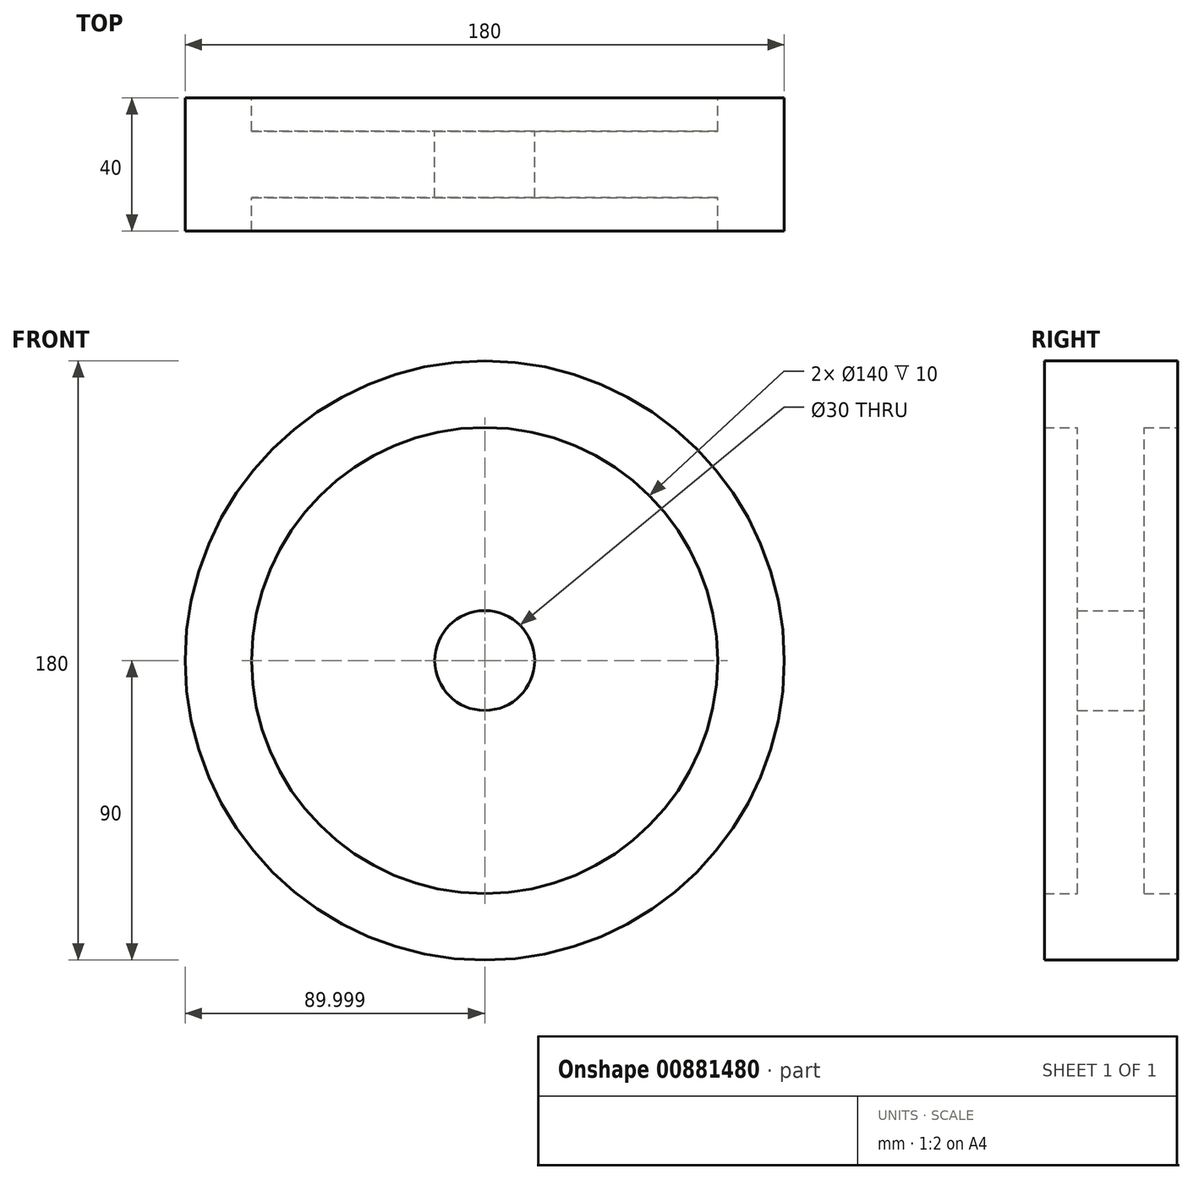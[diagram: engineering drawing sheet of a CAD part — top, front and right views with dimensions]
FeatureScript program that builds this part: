
annotation { "Feature Type Name" : "Feature", "Feature Type Description" : "" }
export const myFeature = defineFeature(function(context is Context, id is Id, definition is map)
    precondition{}
    {
        {
            var Q0;
            Q0=qCreatedBy(makeId("Front.planeOp"),FACE);
            var sketch = newSketch(context, id + "F0", { "sketchPlane" : qUnion([Q0])});
            skCircle(sketch, "E0", {"center": v(-22.68, 0) * mm, "radius": 15 * mm});
            skCircle(sketch, "E1", {"center": v(-22.68, 0) * mm, "radius": 90 * mm});
            skCircle(sketch, "E2.0", {"center": v(-22.68, 0) * mm, "radius": 70 * mm});
            skSolve(sketch);
        }
        {
            var Q0;
            Q0 = qSketchRegion(id + "F0", true);
            extrude(context, id + "F1", {"entities" : qUnion([Q0]), "depth" : 20 * mm, "offsetDistance" : 25 * mm, "hasSecondDirection" : true, "secondDirectionOppositeDirection" : true, "secondDirectionDepth" : 20 * mm});
        }
        {
            var Q0;
            Q0=makeQuery(id+"F0.imprint","IMPRINT",FACE,{"disambiguationData":[TD([[makeQuery(id+"F0.imprint","IMPRINT",EDGE,{"derivedFrom":sQuery(id+"F0.wireOp",EDGE,"E0")}),-1.0]])]});
            extrude(context, id + "F2", {"entities" : qUnion([Q0]), "operationType" : NewBodyOperationType.ADD, "depth" : 10 * mm, "offsetDistance" : 25 * mm, "hasSecondDirection" : true, "secondDirectionOppositeDirection" : true, "secondDirectionDepth" : 10 * mm});
        }
    });
